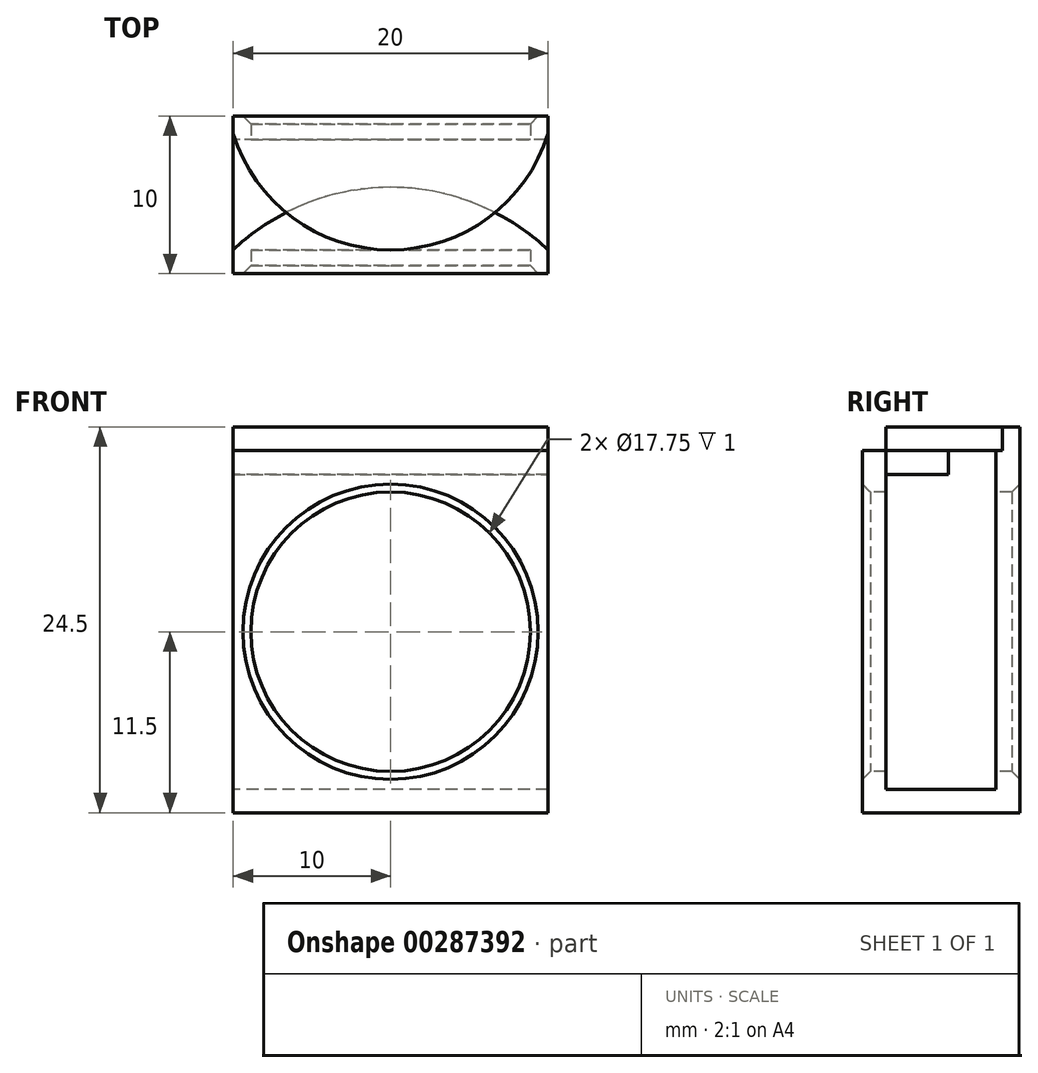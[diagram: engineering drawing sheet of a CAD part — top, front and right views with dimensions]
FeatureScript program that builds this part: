
annotation { "Feature Type Name" : "Feature", "Feature Type Description" : "" }
export const myFeature = defineFeature(function(context is Context, id is Id, definition is map)
    precondition{}
    {
        {
            var Q0;
            Q0=qCreatedBy(makeId("Right.planeOp"),FACE);
            var sketch = newSketch(context, id + "F0", { "sketchPlane" : qUnion([Q0])});
            skLineSegment(sketch, "E0.bottom", {"start": v(3.5, 10) * mm, "end": v(-3.5, 10) * mm});
            skLineSegment(sketch, "E0.top", {"start": v(3.5, -10) * mm, "end": v(-3.5, -10) * mm});
            skLineSegment(sketch, "E0.left", {"start": v(3.5, 10) * mm, "end": v(3.5, -10) * mm});
            skLineSegment(sketch, "E0.right", {"start": v(-3.5, 10) * mm, "end": v(-3.5, -10) * mm});
            skPoint(sketch, "E0.middle", {"position": v(0, 0) * mm});
            skLineSegment(sketch, "E1.0", {"start": v(5, 11.5) * mm, "end": v(-5, 11.5) * mm});
            skLineSegment(sketch, "E1.1", {"start": v(5, 11.5) * mm, "end": v(5, -11.5) * mm});
            skLineSegment(sketch, "E1.2", {"start": v(5, -11.5) * mm, "end": v(-5, -11.5) * mm});
            skLineSegment(sketch, "E1.3", {"start": v(-5, 11.5) * mm, "end": v(-5, -11.5) * mm});
            skLineSegment(sketch, "E2", {"start": v(3.5, 11.5) * mm, "end": v(3.5, 10) * mm});
            skLineSegment(sketch, "E3", {"start": v(5, 11.5) * mm, "end": v(5, 13) * mm});
            skLineSegment(sketch, "E4", {"start": v(5, 13) * mm, "end": v(-3.5, 13) * mm});
            skLineSegment(sketch, "E5", {"start": v(-3.5, 13) * mm, "end": v(-3.5, 11.5) * mm});
            skLineSegment(sketch, "E6", {"start": v(3.5, 10) * mm, "end": v(3.5, 11.5) * mm});
            skSolve(sketch);
        }
        {
            var Q0;
            Q0=qCreatedBy(makeId("Front.planeOp"),FACE);
            var sketch = newSketch(context, id + "F1", { "sketchPlane" : qUnion([Q0])});
            skCircle(sketch, "E7", {"center": v(0, 0) * mm, "radius": 8.88 * mm});
            skSolve(sketch);
        }
        {
            var Q0;
            Q0=makeQuery(id+"F0.imprint","IMPRINT",FACE,{"disambiguationData":[TD([[makeQuery(id+"F0.imprint","IMPRINT",EDGE,{"derivedFrom":sQuery(id+"F0.wireOp",EDGE,"E0.bottom")}),-1.0]])]});
            var Q1;
            {var subQ0=sQuery(id+"F0.wireOp",EDGE,"E3");Q1=makeQuery(id+"F0.imprint","IMPRINT",FACE,{"disambiguationData":[TD([[makeQuery(id+"F0.imprint","IMPRINT",EDGE,{"derivedFrom":subQ0}),1.0]])]});}
            extrude(context, id + "F2", {"entities" : qUnion([Q0, Q1]), "depth" : 10 * mm, "hasSecondDirection" : true, "secondDirectionOppositeDirection" : true, "secondDirectionDepth" : 10 * mm});
        }
        {
            var Q0;
            Q0=makeQuery(id+"F1.imprint","IMPRINT",FACE,{"disambiguationData":[TD([[makeQuery(id+"F1.imprint","IMPRINT",EDGE,{"derivedFrom":sQuery(id+"F1.wireOp",EDGE,"E7")}),1.0]])]});
            extrude(context, id + "F3", {"entities" : qUnion([Q0]), "operationType" : NewBodyOperationType.REMOVE, "oppositeDirection" : true, "depth" : 25 * mm, "hasSecondDirection" : true, "secondDirectionOppositeDirection" : false, "secondDirectionDepth" : 25 * mm});
        }
        {
            var Q0;
            Q0=makeQuery(id+"F2.opExtrude","SWEPT_FACE",FACE,{"disambiguationData":[OSD([sQuery(id+"F0.wireOp",EDGE,"E4")])]});
            var sketch = newSketch(context, id + "F4", { "sketchPlane" : qUnion([Q0])});
            skLineSegment(sketch, "E8", {"start": v(-10, 5) * mm, "end": v(-10, -3.5) * mm});
            skLineSegment(sketch, "E9", {"start": v(-10, -3.5) * mm, "end": v(0, -3.5) * mm});
            skLineSegment(sketch, "E10", {"start": v(0, -3.5) * mm, "end": v(10, -3.5) * mm});
            skLineSegment(sketch, "E11", {"start": v(10, -3.5) * mm, "end": v(10, 5) * mm});
            skPoint(sketch, "E12", {"position": v(-10, 3.9) * mm});
            skPoint(sketch, "E13", {"position": v(10, 3.9) * mm});
            skArc(sketch, "E14", {"start": v(-10, 3.9) * mm, "mid": v(0, -3.5) * mm, "end": v(10, 3.9) * mm});
            skSolve(sketch);
        }
        {
            var Q0;
            {var subQ0=sQuery(id+"F4.wireOp",EDGE,"E9");Q0=makeQuery(id+"F4.imprint","IMPRINT",FACE,{"disambiguationData":[TD([[makeQuery(id+"F4.imprint","IMPRINT",EDGE,{"derivedFrom":subQ0}),-1.0]])]});}
            var Q1;
            {var subQ0=sQuery(id+"F4.wireOp",EDGE,"E10");Q1=makeQuery(id+"F4.imprint","IMPRINT",FACE,{"disambiguationData":[TD([[makeQuery(id+"F4.imprint","IMPRINT",EDGE,{"derivedFrom":subQ0}),-1.0]])]});}
            extrude(context, id + "F5", {"entities" : qUnion([Q0, Q1]), "operationType" : NewBodyOperationType.REMOVE, "oppositeDirection" : true, "depth" : 1.5 * mm});
        }
        {
            var Q0;
            Q0=makeQuery(id+"F2.opExtrude","SWEPT_FACE",FACE,{"disambiguationData":[OSD([sQuery(id+"F0.wireOp",EDGE,"E0.bottom")])]});
            var sketch = newSketch(context, id + "F6", { "sketchPlane" : qUnion([Q0])});
            skArc(sketch, "E15", {"start": v(-10, 3.5) * mm, "mid": v(0, -0.48) * mm, "end": v(10, 3.5) * mm});
            skLineSegment(sketch, "E16", {"start": v(10, 3.5) * mm, "end": v(10, -3.5) * mm});
            skLineSegment(sketch, "E17", {"start": v(10, -3.5) * mm, "end": v(-10, -3.5) * mm});
            skLineSegment(sketch, "E18", {"start": v(-10, -3.5) * mm, "end": v(-10, 3.5) * mm});
            skSolve(sketch);
        }
        {
            var Q0;
            Q0 = qSketchRegion(id + "F6", true);
            extrude(context, id + "F7", {"entities" : qUnion([Q0]), "operationType" : NewBodyOperationType.REMOVE, "oppositeDirection" : true, "depth" : 1.5 * mm});
        }
        {
            var Q0;
            Q0=makeQuery(id+"F3.boolean.opBoolean","INTERSECT",EDGE,{"derivedFrom":[makeQuery(id+"F2.opExtrude","SWEPT_FACE",FACE,{"disambiguationData":[OSD([sQuery(id+"F0.wireOp",EDGE,"E1.3")])]}),makeQuery(id+"F3.opExtrude","SWEPT_FACE",FACE,{"disambiguationData":[OSD([sQuery(id+"F1.wireOp",EDGE,"E7")])]})]});
            var Q1;
            Q1=makeQuery(id+"F3.boolean.opBoolean","INTERSECT",EDGE,{"derivedFrom":[makeQuery(id+"F2.opExtrude","SWEPT_FACE",FACE,{"disambiguationData":[OSD([sQuery(id+"F0.wireOp",EDGE,"E1.1"),sQuery(id+"F0.wireOp",EDGE,"E3")])]}),makeQuery(id+"F3.opExtrude","SWEPT_FACE",FACE,{"disambiguationData":[OSD([sQuery(id+"F1.wireOp",EDGE,"E7")])]})]});
            chamfer(context, id + "F8", {"entities" : qUnion([Q0, Q1]), "width" : .5 * mm, "tangentPropagation" : true});
        }
    });
